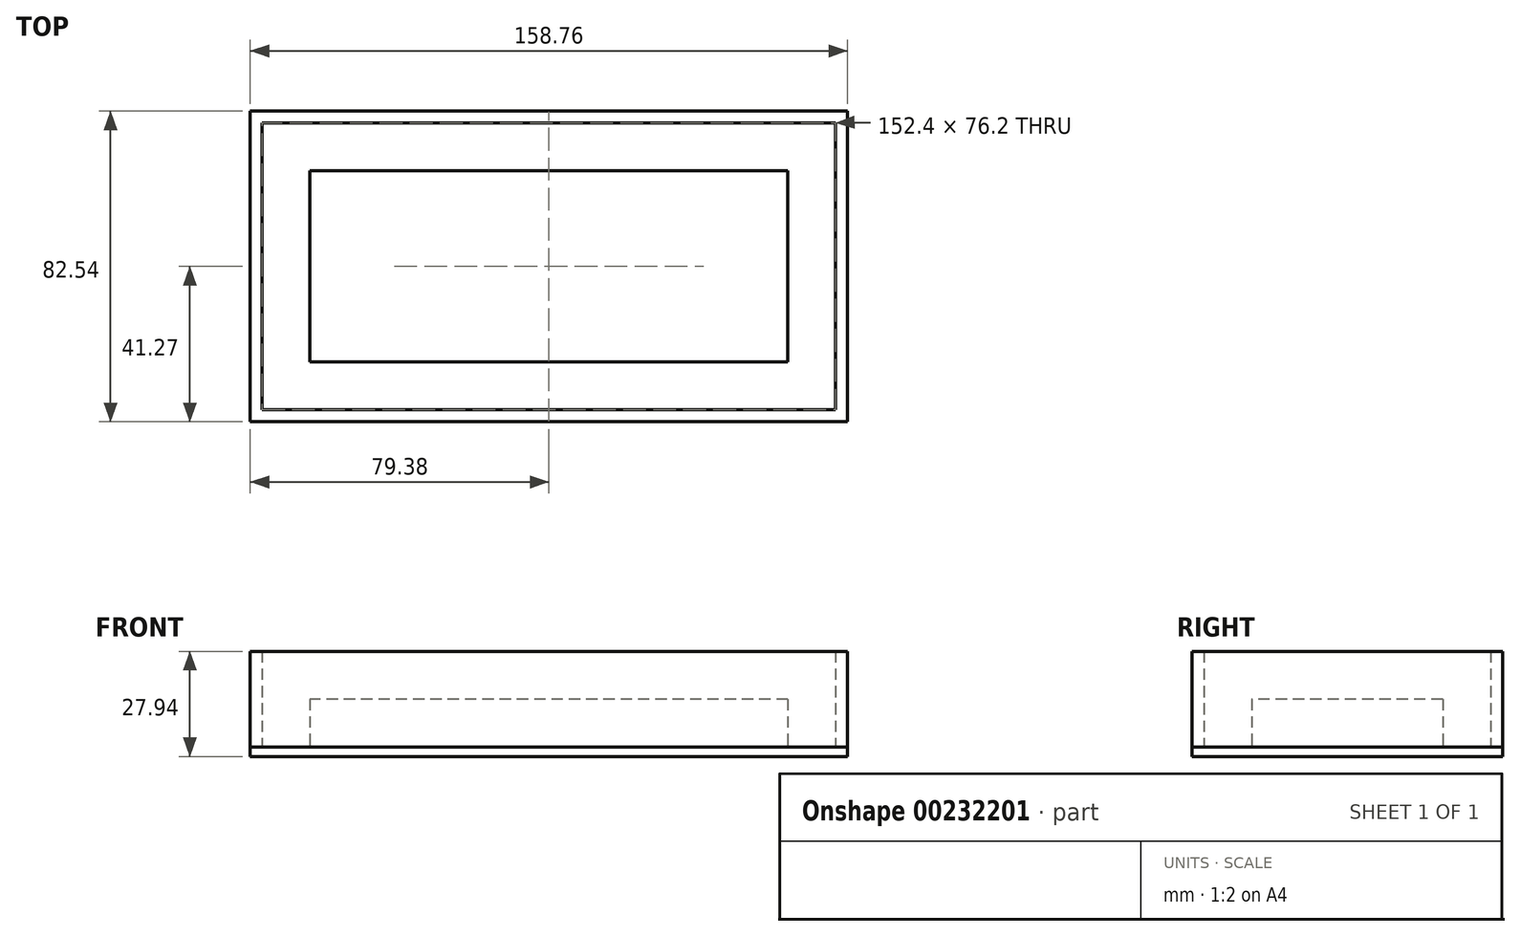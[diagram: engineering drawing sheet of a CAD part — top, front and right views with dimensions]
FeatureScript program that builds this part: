
annotation { "Feature Type Name" : "Feature", "Feature Type Description" : "" }
export const myFeature = defineFeature(function(context is Context, id is Id, definition is map)
    precondition{}
    {
        {
            var Q0;
            Q0=qCreatedBy(makeId("Top.planeOp"),FACE);
            var sketch = newSketch(context, id + "F0", { "sketchPlane" : qUnion([Q0])});
            skLineSegment(sketch, "E0.bottom", {"start": v(76.2, 38.1) * mm, "end": v(-76.2, 38.1) * mm});
            skLineSegment(sketch, "E0.top", {"start": v(76.2, -38.1) * mm, "end": v(-76.2, -38.1) * mm});
            skLineSegment(sketch, "E0.left", {"start": v(76.2, 38.1) * mm, "end": v(76.2, -38.1) * mm});
            skLineSegment(sketch, "E0.right", {"start": v(-76.2, 38.1) * mm, "end": v(-76.2, -38.1) * mm});
            skPoint(sketch, "E0.middle", {"position": v(0, 0) * mm});
            skLineSegment(sketch, "E1.bottom", {"start": v(63.5, 25.4) * mm, "end": v(-63.5, 25.4) * mm});
            skLineSegment(sketch, "E1.top", {"start": v(63.5, -25.4) * mm, "end": v(-63.5, -25.4) * mm});
            skLineSegment(sketch, "E1.left", {"start": v(63.5, 25.4) * mm, "end": v(63.5, -25.4) * mm});
            skLineSegment(sketch, "E1.right", {"start": v(-63.5, 25.4) * mm, "end": v(-63.5, -25.4) * mm});
            skLineSegment(sketch, "E2.bottom", {"start": v(79.38, 41.28) * mm, "end": v(-79.38, 41.27) * mm});
            skLineSegment(sketch, "E2.top", {"start": v(79.38, -41.27) * mm, "end": v(-79.37, -41.28) * mm});
            skLineSegment(sketch, "E2.left", {"start": v(79.37, 41.28) * mm, "end": v(79.38, -41.27) * mm});
            skLineSegment(sketch, "E2.right", {"start": v(-79.38, 41.27) * mm, "end": v(-79.37, -41.28) * mm});
            skSolve(sketch);
        }
        {
            var Q0;
            Q0=makeQuery(id+"F0.imprint","IMPRINT",FACE,{"disambiguationData":[TD([[makeQuery(id+"F0.imprint","IMPRINT",EDGE,{"derivedFrom":sQuery(id+"F0.wireOp",EDGE,"E0.bottom")}),-1.0]])]});
            extrude(context, id + "F1", {"entities" : qUnion([Q0]), "depth" : 25.4 * mm});
        }
        {
            var Q0;
            Q0=makeQuery(id+"F0.imprint","IMPRINT",FACE,{"disambiguationData":[TD([[makeQuery(id+"F0.imprint","IMPRINT",EDGE,{"derivedFrom":sQuery(id+"F0.wireOp",EDGE,"E1.bottom")}),1.0]])]});
            extrude(context, id + "F2", {"entities" : qUnion([Q0]), "depth" : 12.7 * mm});
        }
        {
            var Q0;
            Q0=qCreatedBy(makeId("Top.planeOp"),FACE);
            var sketch = newSketch(context, id + "F3", { "sketchPlane" : qUnion([Q0])});
            skLineSegment(sketch, "E3.bottom", {"start": v(79.38, -41.28) * mm, "end": v(-79.38, -41.28) * mm});
            skLineSegment(sketch, "E3.top", {"start": v(79.38, 41.28) * mm, "end": v(-79.38, 41.28) * mm});
            skLineSegment(sketch, "E3.left", {"start": v(79.38, -41.28) * mm, "end": v(79.38, 41.28) * mm});
            skLineSegment(sketch, "E3.right", {"start": v(-79.38, -41.28) * mm, "end": v(-79.38, 41.28) * mm});
            skPoint(sketch, "E3.middle", {"position": v(0, 0) * mm});
            skSolve(sketch);
        }
        {
            var Q0;
            Q0 = qSketchRegion(id + "F3", true);
            extrude(context, id + "F4", {"entities" : qUnion([Q0]), "oppositeDirection" : true, "depth" : 2.54 * mm});
        }
    });
